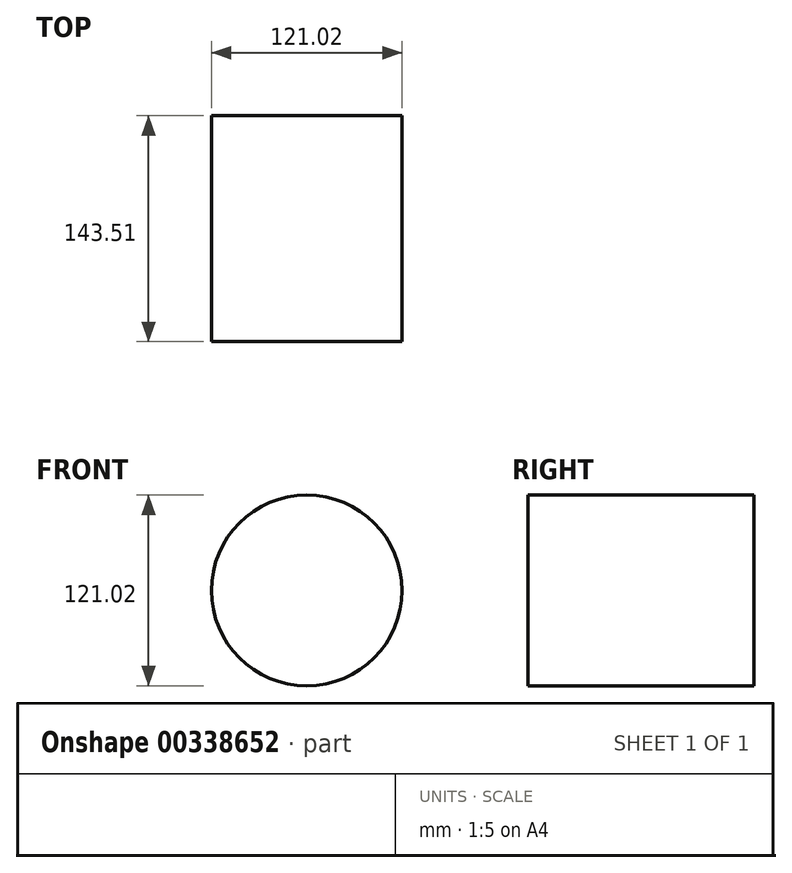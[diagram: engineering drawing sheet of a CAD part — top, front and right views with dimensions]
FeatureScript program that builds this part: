
annotation { "Feature Type Name" : "Feature", "Feature Type Description" : "" }
export const myFeature = defineFeature(function(context is Context, id is Id, definition is map)
    precondition{}
    {
        {
            var Q0;
            Q0=qCreatedBy(makeId("Front.planeOp"),FACE);
            var sketch = newSketch(context, id + "F0", { "sketchPlane" : qUnion([Q0])});
            skCircle(sketch, "E0", {"center": v(0, 0) * mm, "radius": 60.51 * mm});
            skSolve(sketch);
        }
        {
            var Q0;
            Q0 = qSketchRegion(id + "F0", true);
            extrude(context, id + "F1", {"entities" : qUnion([Q0]), "depth" : 143.5 * mm, "offsetDistance" : 25.4 * mm});
        }
    });
